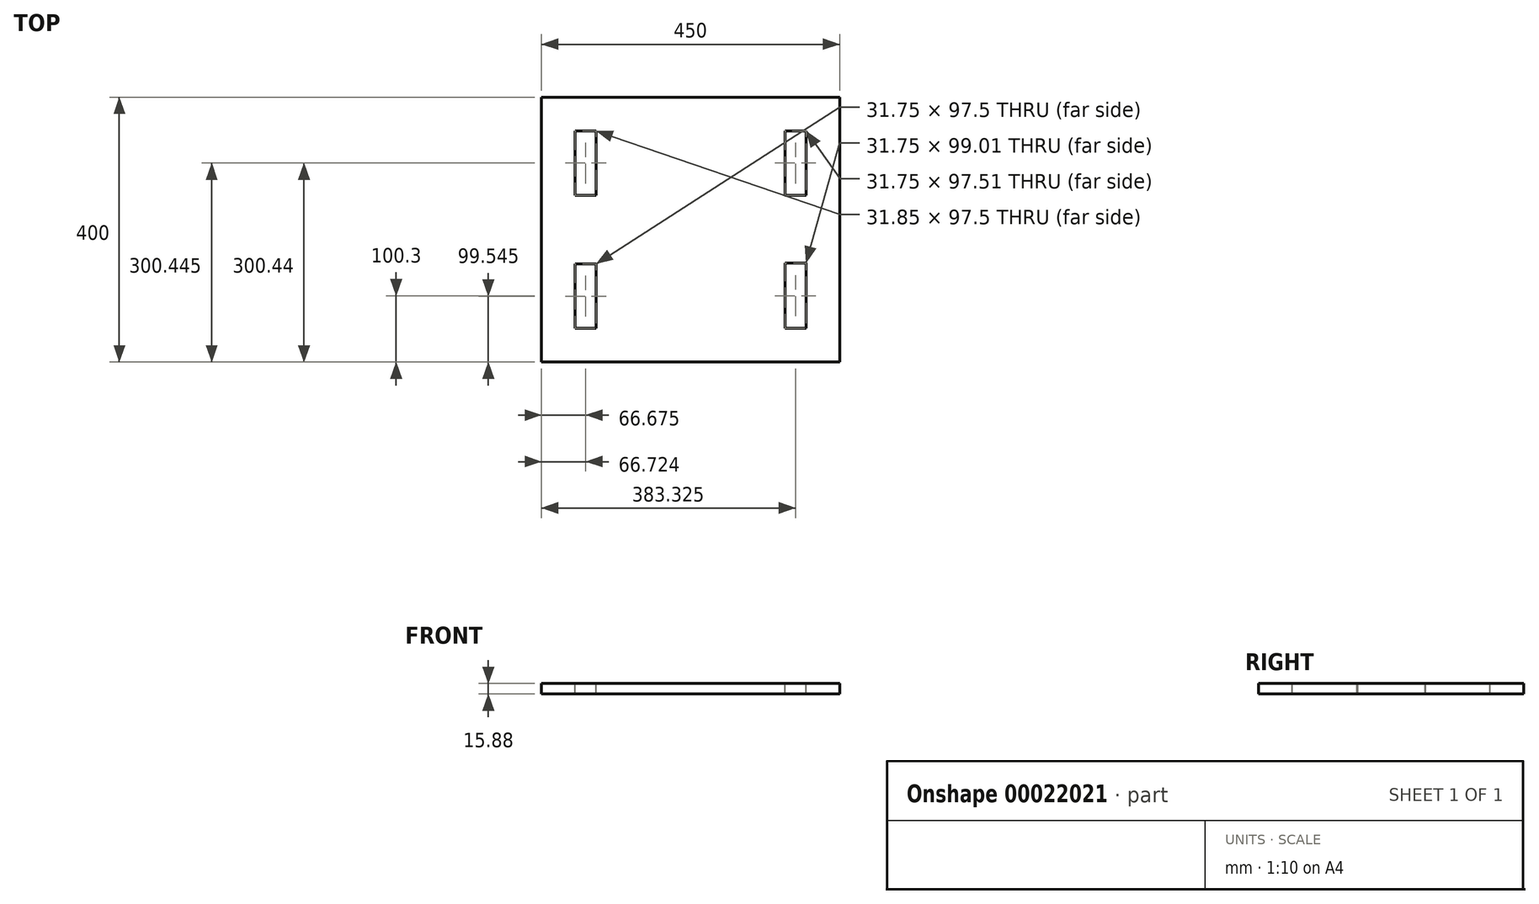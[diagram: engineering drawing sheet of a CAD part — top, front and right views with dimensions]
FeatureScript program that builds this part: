
annotation { "Feature Type Name" : "Feature", "Feature Type Description" : "" }
export const myFeature = defineFeature(function(context is Context, id is Id, definition is map)
    precondition{}
    {
        {
            var Q0;
            Q0=qCreatedBy(makeId("Top.planeOp"),FACE);
            var sketch = newSketch(context, id + "F0", { "sketchPlane" : qUnion([Q0])});
            skLineSegment(sketch, "E0.bottom", {"start": v(-224.55, 174.78) * mm, "end": v(225.45, 174.78) * mm});
            skLineSegment(sketch, "E0.top", {"start": v(-224.55, -225.22) * mm, "end": v(225.45, -225.22) * mm});
            skLineSegment(sketch, "E0.left", {"start": v(-224.55, 174.78) * mm, "end": v(-224.55, -225.22) * mm});
            skLineSegment(sketch, "E0.right", {"start": v(225.45, 174.78) * mm, "end": v(225.45, -225.22) * mm});
            skSolve(sketch);
        }
        {
            var Q0;
            Q0 = qSketchRegion(id + "F0", true);
            extrude(context, id + "F1", {"entities" : qUnion([Q0]), "depth" : 15.88 * mm});
        }
        {
            var Q0;
            Q0=makeQuery(id+"F1.opExtrude","CAP_FACE",FACE,{"disambiguationData":[OSD([sQuery(id+"F0.wireOp",EDGE,"E0.bottom"),sQuery(id+"F0.wireOp",EDGE,"E0.top"),sQuery(id+"F0.wireOp",EDGE,"E0.left"),sQuery(id+"F0.wireOp",EDGE,"E0.right")])],"isStart":false});
            var sketch = newSketch(context, id + "F2", { "sketchPlane" : qUnion([Q0])});
            skLineSegment(sketch, "E1", {"start": v(-173.75, 123.98) * mm, "end": v(-224.55, 123.98) * mm});
            skLineSegment(sketch, "E2", {"start": v(174.65, 123.98) * mm, "end": v(225.45, 123.98) * mm});
            skLineSegment(sketch, "E3.bottom", {"start": v(-173.75, -76.92) * mm, "end": v(-142, -76.92) * mm});
            skLineSegment(sketch, "E3.top", {"start": v(-173.75, -174.42) * mm, "end": v(-142, -174.42) * mm});
            skLineSegment(sketch, "E3.left", {"start": v(-173.75, -76.92) * mm, "end": v(-173.75, -174.42) * mm});
            skLineSegment(sketch, "E3.right", {"start": v(-142, -76.92) * mm, "end": v(-142, -174.42) * mm});
            skLineSegment(sketch, "E4", {"start": v(-173.75, 123.98) * mm, "end": v(-173.65, 26.48) * mm});
            skLineSegment(sketch, "E5", {"start": v(-141.9, 123.98) * mm, "end": v(-141.9, 26.48) * mm});
            skLineSegment(sketch, "E6", {"start": v(-173.75, 123.98) * mm, "end": v(-141.9, 123.98) * mm});
            skLineSegment(sketch, "E7", {"start": v(-173.65, 26.48) * mm, "end": v(-141.9, 26.48) * mm});
            skLineSegment(sketch, "E8", {"start": v(174.65, -75.42) * mm, "end": v(142.9, -75.42) * mm});
            skLineSegment(sketch, "E9", {"start": v(142.9, -75.42) * mm, "end": v(142.9, -174.42) * mm});
            skLineSegment(sketch, "E10", {"start": v(142.9, -75.42) * mm, "end": v(174.65, -75.42) * mm});
            skLineSegment(sketch, "E11", {"start": v(174.65, 26.46) * mm, "end": v(142.9, 26.46) * mm});
            skLineSegment(sketch, "E12", {"start": v(142.9, 26.46) * mm, "end": v(142.9, 123.98) * mm});
            skLineSegment(sketch, "E13", {"start": v(142.9, -174.42) * mm, "end": v(174.65, -174.42) * mm});
            skLineSegment(sketch, "E14", {"start": v(174.65, -174.42) * mm, "end": v(225.45, -174.42) * mm});
            skLineSegment(sketch, "E15", {"start": v(174.65, -75.42) * mm, "end": v(174.65, -174.42) * mm});
            skLineSegment(sketch, "E16", {"start": v(174.65, 26.46) * mm, "end": v(174.65, 123.98) * mm});
            skLineSegment(sketch, "E17", {"start": v(142.9, 123.98) * mm, "end": v(174.65, 123.98) * mm});
            skLineSegment(sketch, "E18", {"start": v(-173.75, -174.42) * mm, "end": v(-224.55, -174.42) * mm});
            skLineSegment(sketch, "E19", {"start": v(-142, -174.42) * mm, "end": v(-142, -225.22) * mm});
            skLineSegment(sketch, "E20", {"start": v(-173.75, 123.98) * mm, "end": v(-173.75, 174.78) * mm});
            skLineSegment(sketch, "E21", {"start": v(174.65, 123.98) * mm, "end": v(174.65, 174.78) * mm});
            skLineSegment(sketch, "E22", {"start": v(174.65, -174.42) * mm, "end": v(174.65, -225.22) * mm});
            skSolve(sketch);
        }
        {
            var Q0;
            Q0=makeQuery(id+"F2.imprint","IMPRINT",FACE,{"disambiguationData":[TD([[makeQuery(id+"F2.imprint","IMPRINT",EDGE,{"derivedFrom":sQuery(id+"F2.wireOp",EDGE,"E4")}),1.0]])]});
            var Q1;
            {var subQ1=sQuery(id+"F2.wireOp",EDGE,"E11");Q1=makeQuery(id+"F2.imprint","IMPRINT",FACE,{"disambiguationData":[TD([[makeQuery(id+"F2.imprint","IMPRINT",EDGE,{"derivedFrom":subQ1}),-1.0]])]});}
            extrude(context, id + "F3", {"entities" : qUnion([Q0, Q1]), "operationType" : NewBodyOperationType.REMOVE, "oppositeDirection" : true, "depth" : 25.4 * mm});
        }
        {
            var Q0;
            Q0 = qSketchRegion(id + "F2", true);
            extrude(context, id + "F4", {"entities" : qUnion([Q0]), "operationType" : NewBodyOperationType.REMOVE, "oppositeDirection" : true, "depth" : 25.4 * mm});
        }
    });
